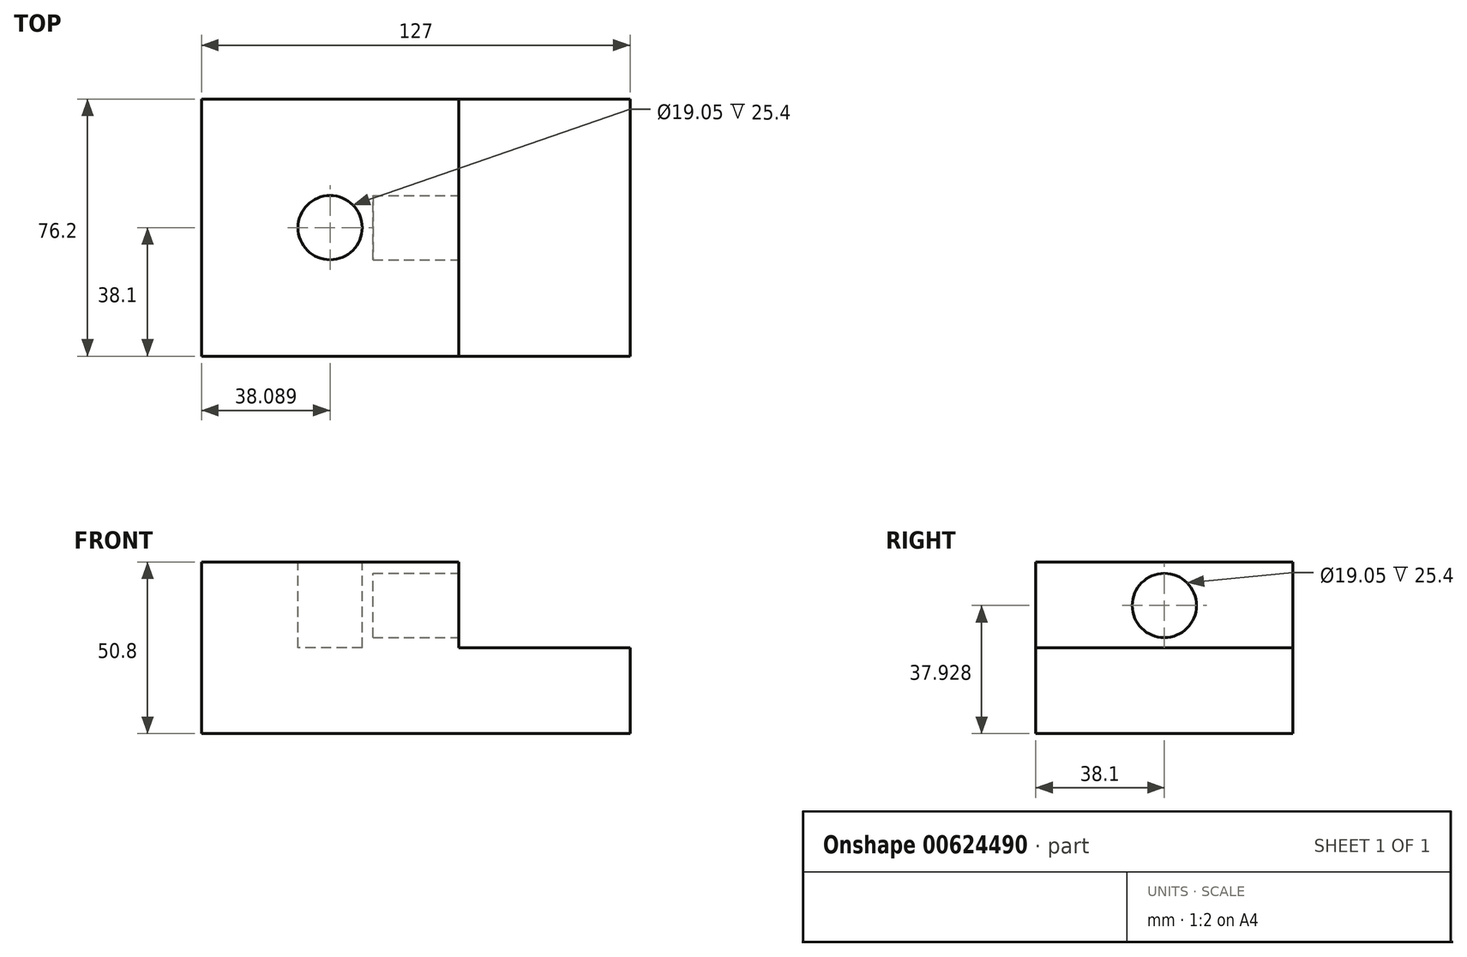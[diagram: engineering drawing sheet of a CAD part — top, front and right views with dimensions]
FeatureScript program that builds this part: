
annotation { "Feature Type Name" : "Feature", "Feature Type Description" : "" }
export const myFeature = defineFeature(function(context is Context, id is Id, definition is map)
    precondition{}
    {
        {
            var Q0;
            Q0=qCreatedBy(makeId("Front.planeOp"),FACE);
            var sketch = newSketch(context, id + "F0", { "sketchPlane" : qUnion([Q0])});
            skLineSegment(sketch, "E0.bottom", {"start": v(0, 0) * mm, "end": v(127, 0) * mm});
            skLineSegment(sketch, "E0.top", {"start": v(0, 50.8) * mm, "end": v(127, 50.8) * mm});
            skLineSegment(sketch, "E0.left", {"start": v(0, 0) * mm, "end": v(0, 50.8) * mm});
            skLineSegment(sketch, "E0.right", {"start": v(127, 0) * mm, "end": v(127, 50.8) * mm});
            skSolve(sketch);
        }
        {
            var Q0;
            Q0=qCreatedBy(makeId("Top.planeOp"),FACE);
            var sketch = newSketch(context, id + "F1", { "sketchPlane" : qUnion([Q0])});
            skLineSegment(sketch, "E1.bottom", {"start": v(0, 0) * mm, "end": v(127, 0) * mm});
            skLineSegment(sketch, "E1.top", {"start": v(0, 76.2) * mm, "end": v(127, 76.2) * mm});
            skLineSegment(sketch, "E1.left", {"start": v(0, 0) * mm, "end": v(0, 76.2) * mm});
            skLineSegment(sketch, "E1.right", {"start": v(127, 0) * mm, "end": v(127, 76.2) * mm});
            skSolve(sketch);
        }
        {
            var Q0;
            Q0=qCreatedBy(makeId("Right.planeOp"),FACE);
            var sketch = newSketch(context, id + "F2", { "sketchPlane" : qUnion([Q0])});
            skLineSegment(sketch, "E2.bottom", {"start": v(0, 0) * mm, "end": v(76.2, 0) * mm});
            skLineSegment(sketch, "E2.top", {"start": v(0, 50.8) * mm, "end": v(76.2, 50.8) * mm});
            skLineSegment(sketch, "E2.left", {"start": v(0, 0) * mm, "end": v(0, 50.8) * mm});
            skLineSegment(sketch, "E2.right", {"start": v(76.2, 0) * mm, "end": v(76.2, 50.8) * mm});
            skSolve(sketch);
        }
        {
            var Q0;
            Q0=makeQuery(id+"F2.imprint","IMPRINT",FACE,{"disambiguationData":[TD([[makeQuery(id+"F2.imprint","IMPRINT",EDGE,{"derivedFrom":sQuery(id+"F2.wireOp",EDGE,"E2.bottom")}),1.0]])]});
            extrude(context, id + "F3", {"entities" : qUnion([Q0]), "depth" : 76.2 * mm, "offsetDistance" : 25.4 * mm});
        }
        {
            var Q0;
            Q0=makeQuery(id+"F1.imprint","IMPRINT",FACE,{"disambiguationData":[TD([[makeQuery(id+"F1.imprint","IMPRINT",EDGE,{"derivedFrom":sQuery(id+"F1.wireOp",EDGE,"E1.bottom")}),1.0]])]});
            extrude(context, id + "F4", {"entities" : qUnion([Q0]), "operationType" : NewBodyOperationType.ADD, "depth" : 25.4 * mm, "offsetDistance" : 25.4 * mm});
        }
        {
            var Q0;
            Q0=makeQuery(id+"F3.opExtrude","SWEPT_FACE",FACE,{"disambiguationData":[OSD([sQuery(id+"F2.wireOp",EDGE,"E2.top")])]});
            var sketch = newSketch(context, id + "F5", { "sketchPlane" : qUnion([Q0])});
            skCircle(sketch, "E3", {"center": v(38.09, 38.1) * mm, "radius": 9.53 * mm});
            skPoint(sketch, "E3.centerSnap0", {"position": v(76.2, 38.1) * mm});
            skSolve(sketch);
        }
        {
            var Q0;
            Q0=makeQuery(id+"F3.opExtrude","CAP_FACE",FACE,{"disambiguationData":[OSD([sQuery(id+"F2.wireOp",EDGE,"E2.bottom"),sQuery(id+"F2.wireOp",EDGE,"E2.top"),sQuery(id+"F2.wireOp",EDGE,"E2.left"),sQuery(id+"F2.wireOp",EDGE,"E2.right")])],"isStart":false});
            var sketch = newSketch(context, id + "F6", { "sketchPlane" : qUnion([Q0])});
            skCircle(sketch, "E4", {"center": v(38.1, 37.93) * mm, "radius": 9.53 * mm});
            skPoint(sketch, "E4.centerSnap0", {"position": v(38.1, 50.8) * mm});
            skSolve(sketch);
        }
        {
            var Q0;
            Q0=makeQuery(id+"F5.imprint","IMPRINT",FACE,{"disambiguationData":[TD([[makeQuery(id+"F5.imprint","IMPRINT",EDGE,{"derivedFrom":sQuery(id+"F5.wireOp",EDGE,"E3")}),1.0]])]});
            extrude(context, id + "F7", {"entities" : qUnion([Q0]), "operationType" : NewBodyOperationType.REMOVE, "oppositeDirection" : true, "depth" : 25.4 * mm, "offsetDistance" : 25.4 * mm});
        }
        {
            var Q0;
            Q0=makeQuery(id+"F6.imprint","IMPRINT",FACE,{"disambiguationData":[TD([[makeQuery(id+"F6.imprint","IMPRINT",EDGE,{"derivedFrom":sQuery(id+"F6.wireOp",EDGE,"E4")}),1.0]])]});
            var sketch = newSketch(context, id + "F8", { "sketchPlane" : qUnion([Q0])});
            skSolve(sketch);
        }
        {
            var Q0;
            Q0 = qSketchRegion(id + "F8", true);
            var Q1;
            Q1=makeQuery(id+"F6.imprint","IMPRINT",FACE,{"disambiguationData":[TD([[makeQuery(id+"F6.imprint","IMPRINT",EDGE,{"derivedFrom":sQuery(id+"F6.wireOp",EDGE,"E4")}),1.0]])]});
            extrude(context, id + "F9", {"entities" : qUnion([Q0, Q1]), "operationType" : NewBodyOperationType.REMOVE, "oppositeDirection" : true, "depth" : 25.4 * mm, "offsetDistance" : 25.4 * mm});
        }
    });
